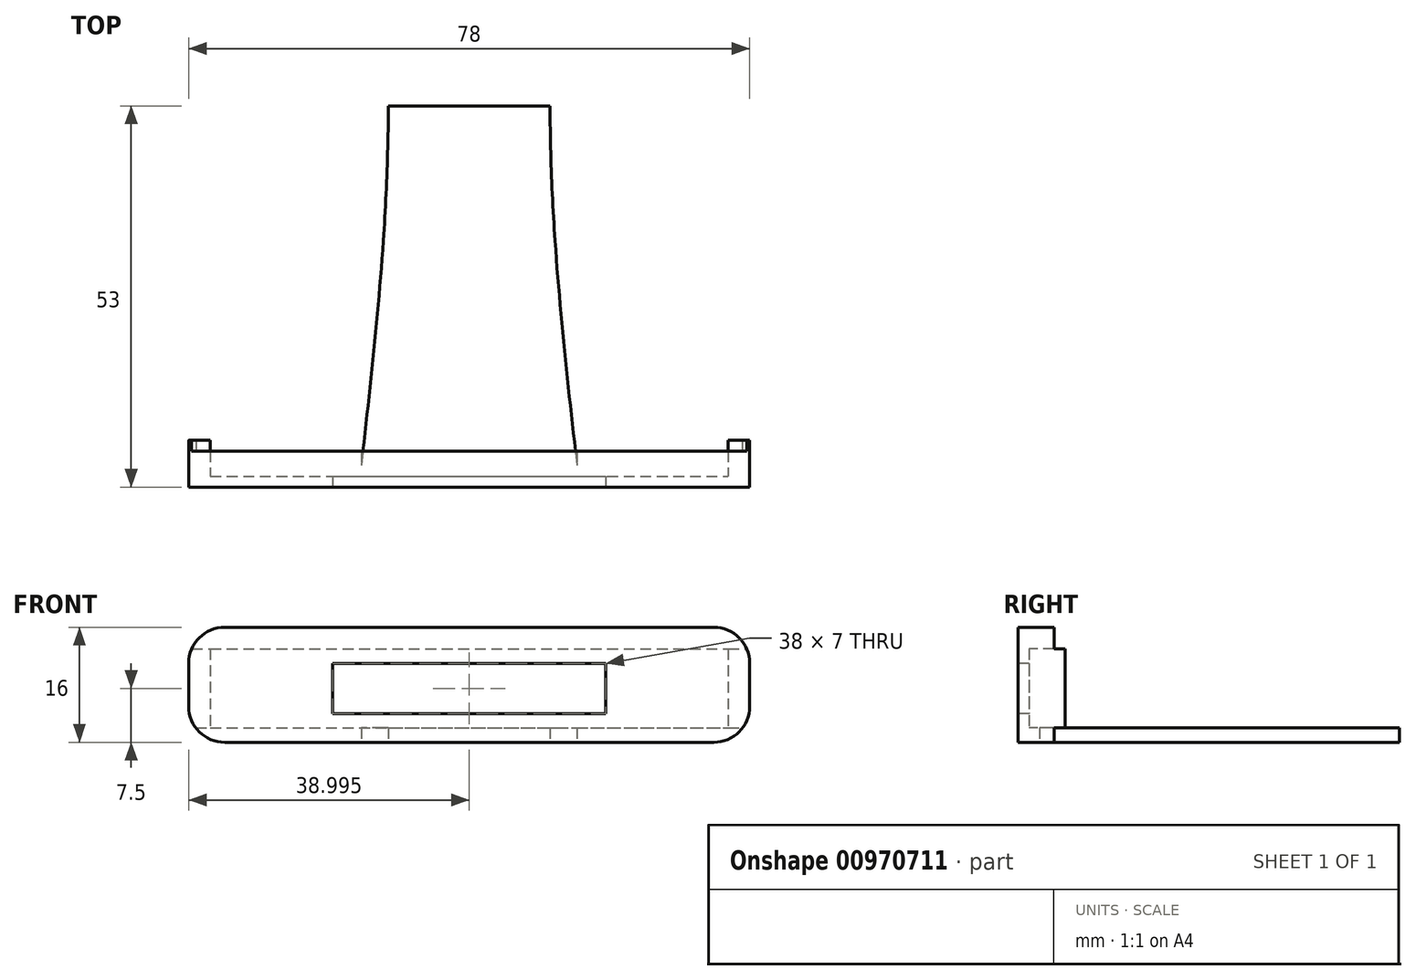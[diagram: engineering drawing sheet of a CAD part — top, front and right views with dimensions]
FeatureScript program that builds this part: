
annotation { "Feature Type Name" : "Feature", "Feature Type Description" : "" }
export const myFeature = defineFeature(function(context is Context, id is Id, definition is map)
    precondition{}
    {
        {
            var Q0;
            Q0=qCreatedBy(makeId("Top.planeOp"),FACE);
            var sketch = newSketch(context, id + "F0", { "sketchPlane" : qUnion([Q0])});
            skLineSegment(sketch, "E0.bottom", {"start": v(-18.4, 18.73) * mm, "end": v(11.6, 18.73) * mm});
            skLineSegment(sketch, "E0.top", {"start": v(-18.4, -31.27) * mm, "end": v(11.6, -31.27) * mm});
            skFitSpline(sketch, "E1", {"points": [v(-18.4, 68.73) * mm, v(-14.65, 18.73) * mm, v(-18.4, -31.27) * mm], "startDerivative": vector(11.25, -100) * mm, "endDerivative": vector(-11.25, -100) * mm});
            skFitSpline(sketch, "E2", {"points": [v(11.6, 68.73) * mm, v(7.85, 18.73) * mm, v(11.6, -31.27) * mm], "startDerivative": vector(-11.25, -100) * mm, "endDerivative": vector(11.25, -100) * mm});
            skPoint(sketch, "E3", {"position": v(-42.4, -31.27) * mm});
            skPoint(sketch, "E4", {"position": v(35.6, -31.27) * mm});
            skPoint(sketch, "E5", {"position": v(-42.4, -34.27) * mm});
            skLineSegment(sketch, "E6.bottom", {"start": v(-42.4, -31.27) * mm, "end": v(35.6, -31.27) * mm});
            skLineSegment(sketch, "E6.top", {"start": v(-42.4, -34.27) * mm, "end": v(35.6, -34.27) * mm});
            skLineSegment(sketch, "E6.left", {"start": v(-42.4, -31.27) * mm, "end": v(-42.4, -34.27) * mm});
            skLineSegment(sketch, "E6.right", {"start": v(35.6, -31.27) * mm, "end": v(35.6, -34.27) * mm});
            skLineSegment(sketch, "E7", {"start": v(-15.35, 0) * mm, "end": v(8.54, 0) * mm});
            skSolve(sketch);
        }
        {
            var Q0;
            {var subQ0=sQuery(id+"F0.wireOp",EDGE,"E1");var subQ1=sQuery(id+"F0.wireOp",EDGE,"E0.bottom");var subQ2=makeQuery(id+"F0.imprint","INTERSECT",VERTEX,{"derivedFrom":[subQ1,subQ0]});Q0=makeQuery(id+"F0.imprint","IMPRINT",FACE,{"disambiguationData":[TD([[makeQuery(id+"F0.imprint","IMPRINT",EDGE,{"disambiguationData":[TD([[subQ2,-1.0]])],"derivedFrom":subQ1}),-1.0]])]});}
            var Q1;
            Q1=makeQuery(id+"F0.imprint","IMPRINT",FACE,{"disambiguationData":[TD([[makeQuery(id+"F0.imprint","IMPRINT",EDGE,{"derivedFrom":sQuery(id+"F0.wireOp",EDGE,"E6.top")}),1.0]])]});
            var Q2;
            {var subQ3=sQuery(id+"F0.wireOp",EDGE,"E7");Q2=makeQuery(id+"F0.imprint","IMPRINT",FACE,{"disambiguationData":[TD([[makeQuery(id+"F0.imprint","IMPRINT",EDGE,{"derivedFrom":subQ3}),-1.0]])]});}
            extrude(context, id + "F1", {"entities" : qUnion([Q0, Q1, Q2]), "depth" : 2 * mm, "offsetDistance" : 25 * mm});
        }
        {
            var Q0;
            Q0=makeQuery(id+"F1.opExtrude","CAP_FACE",FACE,{"disambiguationData":[OSD([sQuery(id+"F0.wireOp",EDGE,"E0.bottom"),sQuery(id+"F0.wireOp",EDGE,"E1"),sQuery(id+"F0.wireOp",EDGE,"E2"),sQuery(id+"F0.wireOp",EDGE,"E6.bottom"),sQuery(id+"F0.wireOp",EDGE,"E6.top"),sQuery(id+"F0.wireOp",EDGE,"E6.left"),sQuery(id+"F0.wireOp",EDGE,"E6.right")])],"isStart":false});
            var sketch = newSketch(context, id + "F2", { "sketchPlane" : qUnion([Q0])});
            skLineSegment(sketch, "E8.bottom", {"start": v(-42.4, -34.27) * mm, "end": v(35.6, -34.27) * mm});
            skLineSegment(sketch, "E8.top", {"start": v(-42.4, -32.77) * mm, "end": v(35.6, -32.77) * mm});
            skLineSegment(sketch, "E8.left", {"start": v(-42.4, -34.27) * mm, "end": v(-42.4, -32.77) * mm});
            skLineSegment(sketch, "E8.right", {"start": v(35.6, -34.27) * mm, "end": v(35.6, -32.77) * mm});
            skSolve(sketch);
        }
        {
            var Q0;
            Q0 = qSketchRegion(id + "F2", true);
            extrude(context, id + "F3", {"entities" : qUnion([Q0]), "operationType" : NewBodyOperationType.ADD, "depth" : 2 * mm, "offsetDistance" : 25 * mm});
        }
        {
            var Q0;
            Q0=makeQuery(id+"F3.opExtrude","CAP_FACE",FACE,{"disambiguationData":[OSD([sQuery(id+"F2.wireOp",EDGE,"E8.bottom"),sQuery(id+"F2.wireOp",EDGE,"E8.top"),sQuery(id+"F2.wireOp",EDGE,"E8.left"),sQuery(id+"F2.wireOp",EDGE,"E8.right")])],"isStart":false});
            var sketch = newSketch(context, id + "F4", { "sketchPlane" : qUnion([Q0])});
            skLineSegment(sketch, "E9.bottom", {"start": v(-42.4, -32.77) * mm, "end": v(-22.4, -32.77) * mm});
            skLineSegment(sketch, "E9.top", {"start": v(-42.4, -34.27) * mm, "end": v(-22.4, -34.27) * mm});
            skLineSegment(sketch, "E9.left", {"start": v(-42.4, -32.77) * mm, "end": v(-42.4, -34.27) * mm});
            skLineSegment(sketch, "E9.right", {"start": v(-22.4, -32.77) * mm, "end": v(-22.4, -34.27) * mm});
            skLineSegment(sketch, "E10.bottom", {"start": v(35.6, -32.77) * mm, "end": v(15.6, -32.77) * mm});
            skLineSegment(sketch, "E10.top", {"start": v(35.6, -34.27) * mm, "end": v(15.6, -34.27) * mm});
            skLineSegment(sketch, "E10.left", {"start": v(35.6, -32.77) * mm, "end": v(35.6, -34.27) * mm});
            skLineSegment(sketch, "E10.right", {"start": v(15.6, -32.77) * mm, "end": v(15.6, -34.27) * mm});
            skSolve(sketch);
        }
        {
            var Q0;
            Q0 = qSketchRegion(id + "F4", true);
            extrude(context, id + "F5", {"entities" : qUnion([Q0]), "operationType" : NewBodyOperationType.ADD, "depth" : 7 * mm, "offsetDistance" : 25 * mm});
        }
        {
            var Q0;
            Q0=makeQuery(id+"F5.opExtrude","CAP_FACE",FACE,{"disambiguationData":[OSD([sQuery(id+"F4.wireOp",EDGE,"E9.bottom"),sQuery(id+"F4.wireOp",EDGE,"E9.top"),sQuery(id+"F4.wireOp",EDGE,"E9.left"),sQuery(id+"F4.wireOp",EDGE,"E9.right")])],"isStart":false});
            var sketch = newSketch(context, id + "F6", { "sketchPlane" : qUnion([Q0])});
            skLineSegment(sketch, "E11.bottom", {"start": v(-42.4, -34.27) * mm, "end": v(35.6, -34.27) * mm});
            skLineSegment(sketch, "E11.top", {"start": v(-42.4, -32.77) * mm, "end": v(35.6, -32.77) * mm});
            skLineSegment(sketch, "E11.left", {"start": v(-42.4, -34.27) * mm, "end": v(-42.4, -32.77) * mm});
            skLineSegment(sketch, "E11.right", {"start": v(35.6, -34.27) * mm, "end": v(35.6, -32.77) * mm});
            skSolve(sketch);
        }
        {
            var Q0;
            Q0 = qSketchRegion(id + "F6", true);
            extrude(context, id + "F7", {"entities" : qUnion([Q0]), "operationType" : NewBodyOperationType.ADD, "depth" : 2 * mm, "offsetDistance" : 25 * mm});
        }
        {
            var Q0;
            Q0=makeQuery(id+"F7.opExtrude","CAP_FACE",FACE,{"disambiguationData":[OSD([sQuery(id+"F6.wireOp",EDGE,"E11.bottom"),sQuery(id+"F6.wireOp",EDGE,"E11.top"),sQuery(id+"F6.wireOp",EDGE,"E11.left"),sQuery(id+"F6.wireOp",EDGE,"E11.right")])],"isStart":false});
            var sketch = newSketch(context, id + "F8", { "sketchPlane" : qUnion([Q0])});
            skLineSegment(sketch, "E12.bottom", {"start": v(-42.4, -34.27) * mm, "end": v(35.6, -34.27) * mm});
            skLineSegment(sketch, "E12.top", {"start": v(-42.4, -31.27) * mm, "end": v(35.6, -31.27) * mm});
            skLineSegment(sketch, "E12.left", {"start": v(-42.4, -34.27) * mm, "end": v(-42.4, -31.27) * mm});
            skLineSegment(sketch, "E12.right", {"start": v(35.6, -34.27) * mm, "end": v(35.6, -31.27) * mm});
            skSolve(sketch);
        }
        {
            var Q0;
            Q0 = qSketchRegion(id + "F8", true);
            extrude(context, id + "F9", {"entities" : qUnion([Q0]), "operationType" : NewBodyOperationType.ADD, "depth" : 3 * mm, "offsetDistance" : 25 * mm});
        }
        {
            var Q0;
            Q0=makeQuery(id+"F9.opExtrude","SWEPT_FACE",FACE,{"disambiguationData":[OSD([sQuery(id+"F8.wireOp",EDGE,"E12.top")])]});
            extrude(context, id + "F10", {"entities" : qUnion([Q0]), "operationType" : NewBodyOperationType.ADD, "depth" : 2 * mm, "offsetDistance" : 25 * mm});
        }
        {
            var Q0;
            {var subQ0=sQuery(id+"F0.wireOp",EDGE,"E6.bottom");Q0=makeQuery(id+"F1.opExtrude","SWEPT_FACE",FACE,{"disambiguationData":[OSD([subQ0]),TDD([makeQuery(id+"F0.imprint","IMPRINT",EDGE,{"disambiguationData":[TD([[makeQuery(id+"F0.imprint","INTERSECT",VERTEX,{"derivedFrom":[sQuery(id+"F0.wireOp",EDGE,"E2"),subQ0]}),-1.0]])],"derivedFrom":subQ0})])]});}
            var Q1;
            {var subQ0=sQuery(id+"F0.wireOp",EDGE,"E6.bottom");Q1=makeQuery(id+"F1.opExtrude","SWEPT_FACE",FACE,{"disambiguationData":[OSD([subQ0]),TDD([makeQuery(id+"F0.imprint","IMPRINT",EDGE,{"disambiguationData":[TD([[makeQuery(id+"F0.imprint","INTERSECT",VERTEX,{"derivedFrom":[sQuery(id+"F0.wireOp",EDGE,"E1"),subQ0]}),1.0]])],"derivedFrom":subQ0})])]});}
            extrude(context, id + "F11", {"entities" : qUnion([Q0, Q1]), "operationType" : NewBodyOperationType.ADD, "depth" : 2 * mm, "offsetDistance" : 25 * mm});
        }
        {
            var Q0;
            Q0=makeQuery(id+"F7.boolean.opBoolean","MERGE",FACE,{"derivedFrom":[makeQuery(id+"F5.boolean.opBoolean","MERGE",FACE,{"derivedFrom":[makeQuery(id+"F3.opExtrude","SWEPT_FACE",FACE,{"disambiguationData":[OSD([sQuery(id+"F2.wireOp",EDGE,"E8.top")])]}),makeQuery(id+"F5.opExtrude","SWEPT_FACE",FACE,{"disambiguationData":[OSD([sQuery(id+"F4.wireOp",EDGE,"E9.bottom")])]}),makeQuery(id+"F5.opExtrude","SWEPT_FACE",FACE,{"disambiguationData":[OSD([sQuery(id+"F4.wireOp",EDGE,"E10.bottom")])]})]}),makeQuery(id+"F7.opExtrude","SWEPT_FACE",FACE,{"disambiguationData":[OSD([sQuery(id+"F6.wireOp",EDGE,"E11.top")])]})]});
            var sketch = newSketch(context, id + "F12", { "sketchPlane" : qUnion([Q0])});
            skLineSegment(sketch, "E13.bottom", {"start": v(42.4, 13) * mm, "end": v(39.4, 13) * mm});
            skLineSegment(sketch, "E13.top", {"start": v(42.4, 2) * mm, "end": v(39.4, 2) * mm});
            skLineSegment(sketch, "E13.left", {"start": v(42.4, 13) * mm, "end": v(42.4, 2) * mm});
            skLineSegment(sketch, "E13.right", {"start": v(39.4, 13) * mm, "end": v(39.4, 2) * mm});
            skLineSegment(sketch, "E14.bottom", {"start": v(-35.6, 13) * mm, "end": v(-32.6, 13) * mm});
            skLineSegment(sketch, "E14.top", {"start": v(-35.6, 2) * mm, "end": v(-32.6, 2) * mm});
            skLineSegment(sketch, "E14.left", {"start": v(-35.6, 13) * mm, "end": v(-35.6, 2) * mm});
            skLineSegment(sketch, "E14.right", {"start": v(-32.6, 13) * mm, "end": v(-32.6, 2) * mm});
            skSolve(sketch);
        }
        {
            var Q0;
            Q0 = qSketchRegion(id + "F12", true);
            extrude(context, id + "F13", {"entities" : qUnion([Q0]), "operationType" : NewBodyOperationType.ADD, "depth" : 5 * mm, "offsetDistance" : 25 * mm});
        }
        {
            var Q0;
            {var subQ0=sQuery(id+"F8.wireOp",EDGE,"E12.right");var subQ1=sQuery(id+"F8.wireOp",EDGE,"E12.top");Q0=makeQuery(id+"F10.boolean.opBoolean","MERGE",EDGE,{"derivedFrom":[makeQuery(id+"F9.opExtrude","CAP_EDGE",EDGE,{"disambiguationData":[OSD([subQ0])],"isStart":false}),makeQuery(id+"F10.opExtrude","SWEPT_EDGE",EDGE,{"disambiguationData":[OSD([subQ1,subQ0]),TDD([makeQuery(id+"F9.opExtrude","CAP_VERTEX",VERTEX,{"disambiguationData":[OSD([subQ1,subQ0])],"isStart":false})])]})]});}
            var Q1;
            {var subQ0=sQuery(id+"F0.wireOp",EDGE,"E6.right");var subQ1=sQuery(id+"F0.wireOp",EDGE,"E6.bottom");Q1=makeQuery(id+"F11.boolean.opBoolean","MERGE",EDGE,{"derivedFrom":[makeQuery(id+"F1.opExtrude","CAP_EDGE",EDGE,{"disambiguationData":[OSD([subQ0])],"isStart":true}),makeQuery(id+"F11.opExtrude","SWEPT_EDGE",EDGE,{"disambiguationData":[OSD([subQ1,subQ0]),TDD([makeQuery(id+"F1.opExtrude","CAP_VERTEX",VERTEX,{"disambiguationData":[OSD([subQ1,subQ0])],"isStart":true})])]})]});}
            var Q2;
            {var subQ0=sQuery(id+"F0.wireOp",EDGE,"E6.left");var subQ1=sQuery(id+"F0.wireOp",EDGE,"E6.bottom");Q2=makeQuery(id+"F11.boolean.opBoolean","MERGE",EDGE,{"derivedFrom":[makeQuery(id+"F1.opExtrude","CAP_EDGE",EDGE,{"disambiguationData":[OSD([subQ0])],"isStart":true}),makeQuery(id+"F11.opExtrude","SWEPT_EDGE",EDGE,{"disambiguationData":[OSD([subQ1,subQ0]),TDD([makeQuery(id+"F1.opExtrude","CAP_VERTEX",VERTEX,{"disambiguationData":[OSD([subQ1,subQ0])],"isStart":true})])]})]});}
            var Q3;
            {var subQ0=sQuery(id+"F8.wireOp",EDGE,"E12.left");var subQ1=sQuery(id+"F8.wireOp",EDGE,"E12.top");Q3=makeQuery(id+"F10.boolean.opBoolean","MERGE",EDGE,{"derivedFrom":[makeQuery(id+"F9.opExtrude","CAP_EDGE",EDGE,{"disambiguationData":[OSD([subQ0])],"isStart":false}),makeQuery(id+"F10.opExtrude","SWEPT_EDGE",EDGE,{"disambiguationData":[OSD([subQ1,subQ0]),TDD([makeQuery(id+"F9.opExtrude","CAP_VERTEX",VERTEX,{"disambiguationData":[OSD([subQ1,subQ0])],"isStart":false})])]})]});}
            fillet(context, id + "F14", {"entities" : qUnion([Q0, Q1, Q2, Q3]), "radius" : 5 * mm, "tangentPropagation" : true, "allowEdgeOverflow" : false});
        }
    });
